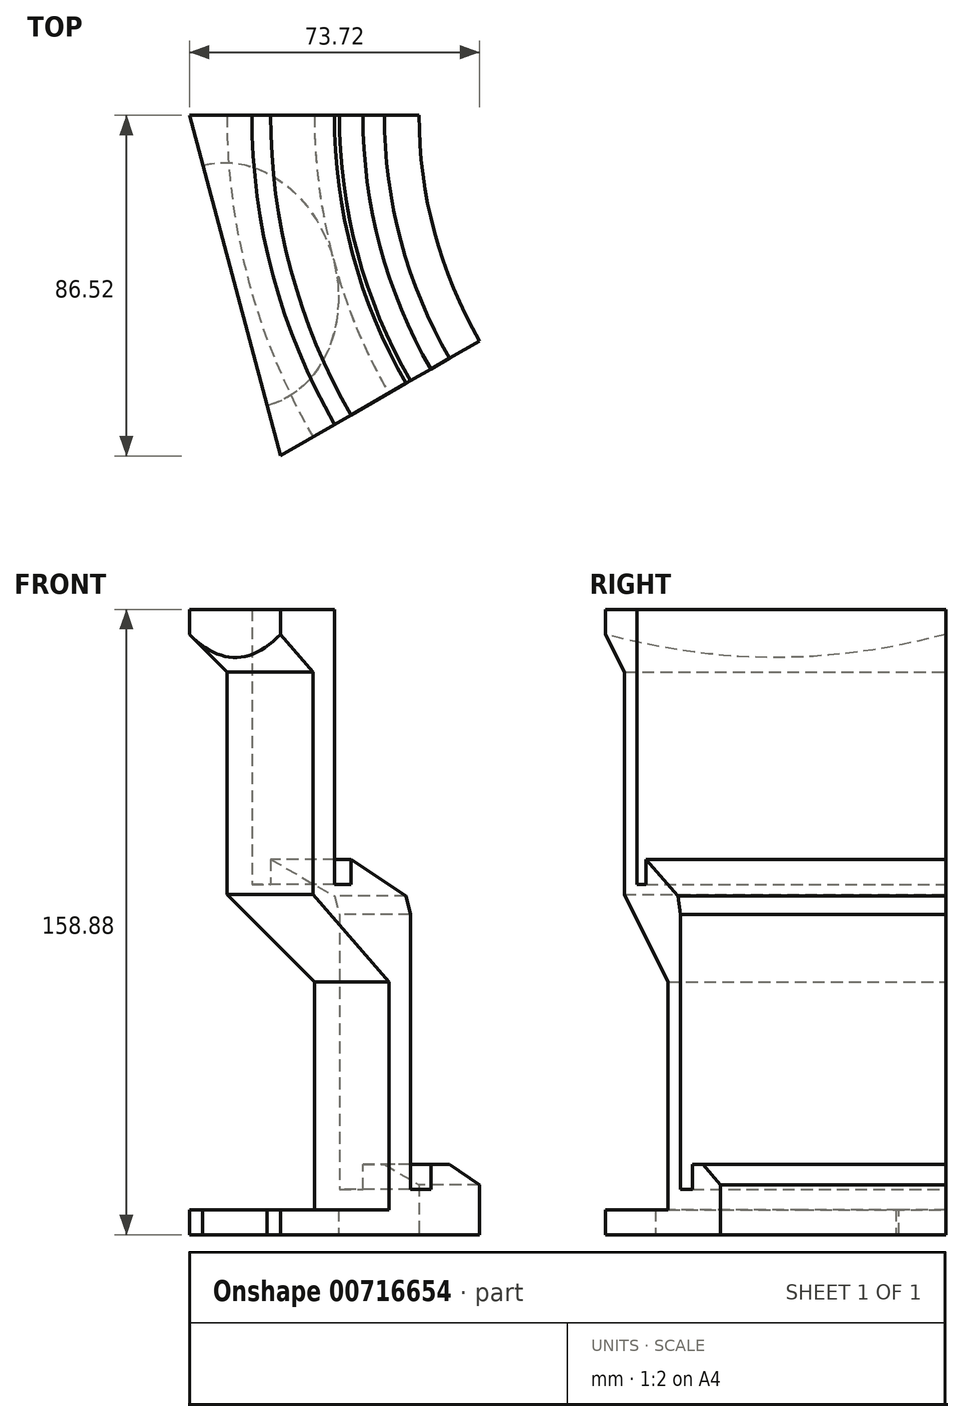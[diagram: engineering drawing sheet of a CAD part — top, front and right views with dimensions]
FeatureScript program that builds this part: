
annotation { "Feature Type Name" : "Feature", "Feature Type Description" : "" }
export const myFeature = defineFeature(function(context is Context, id is Id, definition is map)
    precondition{}
    {
        {
            var Q0;
            Q0=qCreatedBy(makeId("Front.planeOp"),FACE);
            var sketch = newSketch(context, id + "F0", { "sketchPlane" : qUnion([Q0])});
            skLineSegment(sketch, "E0", {"start": v(0, 0) * mm, "end": v(-209.77, 0) * mm, "construction": true});
            skLineSegment(sketch, "E1", {"start": v(-173.04, 0) * mm, "end": v(-173.04, 158.88) * mm});
            skLineSegment(sketch, "E2", {"start": v(-173.04, 158.88) * mm, "end": v(-157.16, 158.88) * mm});
            skLineSegment(sketch, "E3", {"start": v(-157.16, 158.88) * mm, "end": v(-157.16, 89.03) * mm});
            skLineSegment(sketch, "E4", {"start": v(-152.4, 95.38) * mm, "end": v(-136.2, 86.04) * mm});
            skLineSegment(sketch, "E5", {"start": v(-136.2, 86.04) * mm, "end": v(-134.94, 81.3) * mm});
            skLineSegment(sketch, "E6", {"start": v(-134.94, 81.3) * mm, "end": v(-134.94, 11.45) * mm});
            skLineSegment(sketch, "E7", {"start": v(-134.94, 11.45) * mm, "end": v(-128.97, 11.45) * mm});
            skLineSegment(sketch, "E8", {"start": v(-128.97, 11.45) * mm, "end": v(-128.97, 17.8) * mm});
            skLineSegment(sketch, "E9", {"start": v(-128.97, 17.8) * mm, "end": v(-123.5, 17.8) * mm});
            skLineSegment(sketch, "E10", {"start": v(-123.5, 17.8) * mm, "end": v(-114.68, 12.7) * mm});
            skLineSegment(sketch, "E11", {"start": v(-114.68, 12.7) * mm, "end": v(-114.68, 0) * mm});
            skLineSegment(sketch, "E12", {"start": v(-114.68, 0) * mm, "end": v(-173.04, 0) * mm});
            skLineSegment(sketch, "E13", {"start": v(-152.4, 95.38) * mm, "end": v(-152.4, 181.4) * mm, "construction": true});
            skLineSegment(sketch, "E14", {"start": v(-136.2, 86.04) * mm, "end": v(-136.2, 168.43) * mm, "construction": true});
            skLineSegment(sketch, "E15", {"start": v(-152.4, 95.38) * mm, "end": v(-152.4, 89.03) * mm});
            skLineSegment(sketch, "E16", {"start": v(-157.16, 89.03) * mm, "end": v(-152.4, 89.03) * mm});
            skLineSegment(sketch, "E17", {"start": v(-123.5, 17.8) * mm, "end": v(-123.5, 89.88) * mm, "construction": true});
            skLineSegment(sketch, "E18", {"start": v(0, 0) * mm, "end": v(0, 193.3) * mm, "construction": true});
            skLineSegment(sketch, "E19", {"start": v(-173.04, 6.35) * mm, "end": v(-141.29, 6.35) * mm});
            skLineSegment(sketch, "E20", {"start": v(-141.29, 6.35) * mm, "end": v(-141.29, 64.18) * mm});
            skLineSegment(sketch, "E21", {"start": v(-141.29, 64.18) * mm, "end": v(-163.51, 86.4) * mm});
            skLineSegment(sketch, "E22", {"start": v(-173.04, 152.53) * mm, "end": v(-163.51, 143) * mm});
            skLineSegment(sketch, "E23", {"start": v(-163.51, 143) * mm, "end": v(-163.51, 86.4) * mm});
            skSolve(sketch);
        }
        {
            var Q0;
            Q0=makeQuery(id+"F0.imprint","IMPRINT",FACE,{"disambiguationData":[TD([[makeQuery(id+"F0.imprint","IMPRINT",EDGE,{"derivedFrom":sQuery(id+"F0.wireOp",EDGE,"E1")}),-1.0]])]});
            var Q1;
            Q1=sQuery(id+"F0.wireOp",EDGE,"E18");
            revolve(context, id + "F1", {"surfaceOperationType" : NewSurfaceOperationType.NEW, "entities" : qUnion([Q0]), "axis" : qUnion([Q1]), "revolveType" : RevolveType.ONE_DIRECTION, "angle" : 30 * degree});
        }
        {
            var Q0;
            Q0=makeQuery(id+"F1.opRevolve","SWEPT_FACE",FACE,{"disambiguationData":[OSD([sQuery(id+"F0.wireOp",EDGE,"E12")])]});
            var sketch = newSketch(context, id + "F2", { "sketchPlane" : qUnion([Q0])});
            skLineSegment(sketch, "E24", {"start": v(-149.85, 86.52) * mm, "end": v(-173.04, 0) * mm});
            skLineSegment(sketch, "E25", {"start": v(-173.04, 0) * mm, "end": v(-188.04, 0) * mm});
            skLineSegment(sketch, "E26", {"start": v(-188.04, 0) * mm, "end": v(-162.8, 94.16) * mm});
            skLineSegment(sketch, "E27", {"start": v(-162.8, 94.16) * mm, "end": v(-149.85, 86.52) * mm});
            skLineSegment(sketch, "E28", {"start": v(-153.26, 73.82) * mm, "end": v(-128.21, 59.36) * mm});
            skArc(sketch, "E29.0", {"start": v(-122.36, 70.64) * mm, "mid": v(-136.47, 36.57) * mm, "end": v(-141.29, 0) * mm});
            skLineSegment(sketch, "E30", {"start": v(-169.63, 12.7) * mm, "end": v(-140.72, 12.7) * mm});
            skEllipse(sketch, "E31", {"center": v(-161.45, 43.26) * mm, "majorRadius": 31.64 * mm, "minorRadius": 25.85 * mm, "majorAxis": v(0.26, 0.97)});
            skPoint(sketch, "E32", {"position": v(-136.47, 36.57) * mm});
            skSolve(sketch);
        }
        {
            var Q0;
            {var subQ0=sQuery(id+"F2.wireOp",EDGE,"E31");var subQ1=sQuery(id+"F2.wireOp",EDGE,"E26");var subQ2=makeQuery(id+"F2.imprint","INTERSECT",VERTEX,{"disambiguationData":[OD(0.0)],"derivedFrom":[subQ1,subQ0]});Q0=makeQuery(id+"F2.imprint","IMPRINT",FACE,{"disambiguationData":[TD([[makeQuery(id+"F2.imprint","IMPRINT",EDGE,{"disambiguationData":[TD([[subQ2,-1.0]])],"derivedFrom":subQ1}),1.0]])]});}
            var Q1;
            {var subQ0=sQuery(id+"F2.wireOp",EDGE,"E31");var subQ1=sQuery(id+"F2.wireOp",EDGE,"E28");var subQ3=makeQuery(id+"F2.imprint","INTERSECT",VERTEX,{"derivedFrom":[subQ1,subQ0]});Q1=makeQuery(id+"F2.imprint","IMPRINT",FACE,{"disambiguationData":[TD([[makeQuery(id+"F2.imprint","IMPRINT",EDGE,{"disambiguationData":[TD([[subQ3,1.0]])],"derivedFrom":subQ1}),1.0]])]});}
            var Q2;
            {var subQ0=sQuery(id+"F2.wireOp",EDGE,"E31");var subQ1=sQuery(id+"F2.wireOp",EDGE,"E30");var subQ3=makeQuery(id+"F2.imprint","INTERSECT",VERTEX,{"derivedFrom":[subQ1,subQ0]});Q2=makeQuery(id+"F2.imprint","IMPRINT",FACE,{"disambiguationData":[TD([[makeQuery(id+"F2.imprint","IMPRINT",EDGE,{"disambiguationData":[TD([[subQ3,1.0]])],"derivedFrom":subQ1}),-1.0]])]});}
            var Q3;
            {var subQ0=sQuery(id+"F2.wireOp",EDGE,"E31");var subQ1=makeQuery(id+"F2.imprint","INTERSECT",VERTEX,{"derivedFrom":[sQuery(id+"F2.wireOp",EDGE,"E29.0"),subQ0]});Q3=makeQuery(id+"F2.imprint","IMPRINT",FACE,{"disambiguationData":[TD([[makeQuery(id+"F2.imprint","IMPRINT",EDGE,{"disambiguationData":[TD([[subQ1,1.0]])],"derivedFrom":subQ0}),1.0]])]});}
            var Q4;
            {var subQ0=sQuery(id+"F2.wireOp",EDGE,"E25");Q4=makeQuery(id+"F2.imprint","IMPRINT",FACE,{"disambiguationData":[TD([[makeQuery(id+"F2.imprint","IMPRINT",EDGE,{"derivedFrom":subQ0}),-1.0]])]});}
            var Q5;
            {var subQ0=sQuery(id+"F2.wireOp",EDGE,"E27");Q5=makeQuery(id+"F2.imprint","IMPRINT",FACE,{"disambiguationData":[TD([[makeQuery(id+"F2.imprint","IMPRINT",EDGE,{"derivedFrom":subQ0}),-1.0]])]});}
            var Q6;
            {var subQ0=sQuery(id+"F2.wireOp",EDGE,"E24");var subQ4=sQuery(id+"F2.wireOp",EDGE,"E31");var subQ5=makeQuery(id+"F2.imprint","INTERSECT",VERTEX,{"derivedFrom":[subQ0,sQuery(id+"F2.wireOp",EDGE,"E28"),subQ4]});Q6=makeQuery(id+"F2.imprint","IMPRINT",FACE,{"disambiguationData":[TD([[makeQuery(id+"F2.imprint","IMPRINT",EDGE,{"disambiguationData":[TD([[subQ5,-1.0]])],"derivedFrom":subQ4}),-1.0]])]});}
            var Q7;
            {var subQ0=sQuery(id+"F2.wireOp",EDGE,"E24");var subQ4=sQuery(id+"F2.wireOp",EDGE,"E31");var subQ5=makeQuery(id+"F2.imprint","INTERSECT",VERTEX,{"derivedFrom":[subQ0,sQuery(id+"F2.wireOp",EDGE,"E30"),subQ4]});Q7=makeQuery(id+"F2.imprint","IMPRINT",FACE,{"disambiguationData":[TD([[makeQuery(id+"F2.imprint","IMPRINT",EDGE,{"disambiguationData":[TD([[subQ5,1.0]])],"derivedFrom":subQ4}),-1.0]])]});}
            var Q8;
            {var subQ0=sQuery(id+"F2.wireOp",EDGE,"E31");var subQ1=sQuery(id+"F2.wireOp",EDGE,"E24");var subQ2=makeQuery(id+"F2.imprint","INTERSECT",VERTEX,{"derivedFrom":[subQ1,sQuery(id+"F2.wireOp",EDGE,"E28"),subQ0]});Q8=makeQuery(id+"F2.imprint","IMPRINT",FACE,{"disambiguationData":[TD([[makeQuery(id+"F2.imprint","IMPRINT",EDGE,{"disambiguationData":[TD([[subQ2,-1.0]])],"derivedFrom":subQ1}),-1.0]])]});}
            var Q9;
            {var subQ0=sQuery(id+"F2.wireOp",EDGE,"E31");var subQ1=sQuery(id+"F2.wireOp",EDGE,"E26");var subQ2=makeQuery(id+"F2.imprint","INTERSECT",VERTEX,{"disambiguationData":[OD(0.0)],"derivedFrom":[subQ1,subQ0]});Q9=makeQuery(id+"F2.imprint","IMPRINT",FACE,{"disambiguationData":[TD([[makeQuery(id+"F2.imprint","IMPRINT",EDGE,{"disambiguationData":[TD([[subQ2,-1.0]])],"derivedFrom":subQ1}),-1.0]])]});}
            extrude(context, id + "F3", {"entities" : qUnion([Q0, Q1, Q2, Q3, Q4, Q5, Q6, Q7, Q8, Q9]), "operationType" : NewBodyOperationType.REMOVE, "oppositeDirection" : true, "depth" : 25.4 * mm, "offsetDistance" : 25.4 * mm});
        }
        {
            var Q0;
            Q0=makeQuery(id+"F1.opRevolve","SWEPT_FACE",FACE,{"disambiguationData":[OSD([sQuery(id+"F0.wireOp",EDGE,"E2")])]});
            var sketch = newSketch(context, id + "F4", { "sketchPlane" : qUnion([Q0])});
            skLineSegment(sketch, "E33", {"start": v(-173.04, 0) * mm, "end": v(-149.85, -86.52) * mm});
            skLineSegment(sketch, "E34", {"start": v(-149.85, -86.52) * mm, "end": v(-165.36, -86.52) * mm});
            skLineSegment(sketch, "E35", {"start": v(-165.36, -86.52) * mm, "end": v(-187.34, -4.9) * mm});
            skLineSegment(sketch, "E36", {"start": v(-187.34, -4.9) * mm, "end": v(-173.04, 0) * mm});
            skSolve(sketch);
        }
        {
            var Q0;
            Q0 = qSketchRegion(id + "F4", true);
            extrude(context, id + "F5", {"entities" : qUnion([Q0]), "operationType" : NewBodyOperationType.REMOVE, "oppositeDirection" : true, "depth" : 25.4 * mm, "offsetDistance" : 25.4 * mm});
        }
    });
